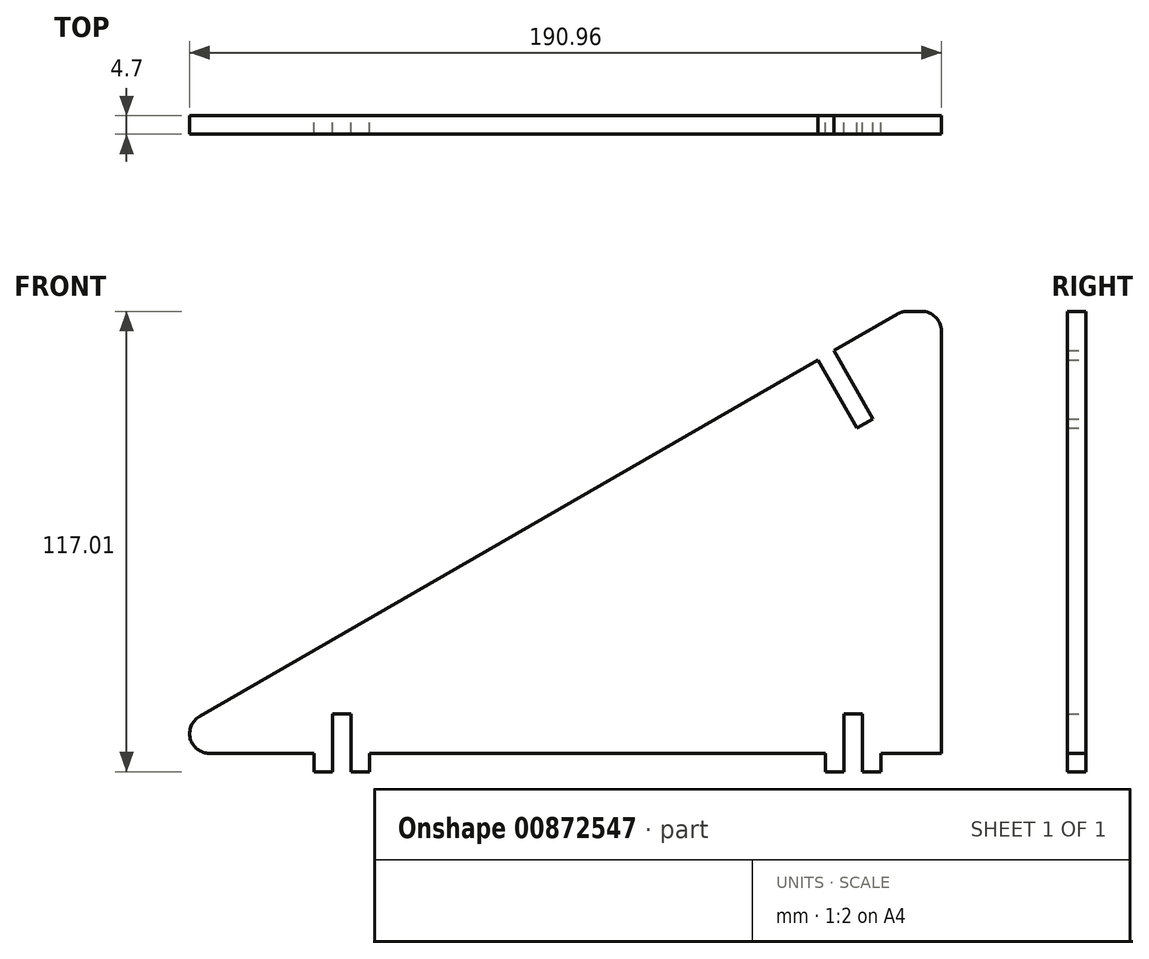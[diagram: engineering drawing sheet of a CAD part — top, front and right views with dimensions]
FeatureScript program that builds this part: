
annotation { "Feature Type Name" : "Feature", "Feature Type Description" : "" }
export const myFeature = defineFeature(function(context is Context, id is Id, definition is map)
    precondition{}
    {
        {
            assignVariable(context, id + "F0", {"name" : "e", "anyValue" : 4.7});
        }
        {
            var Q0;
            Q0=qCreatedBy(makeId("Front.planeOp"),FACE);
            var sketch = newSketch(context, id + "F1", { "sketchPlane" : qUnion([Q0])});
            skLineSegment(sketch, "E0", {"start": v(0, 0) * mm, "end": v(0, 107.3) * mm});
            skLineSegment(sketch, "E1", {"start": v(-5, 112.3) * mm, "end": v(-8.66, 112.3) * mm});
            skLineSegment(sketch, "E2", {"start": v(-11.16, 111.63) * mm, "end": v(-27.32, 102.3) * mm});
            skLineSegment(sketch, "E3", {"start": v(-185.97, 0) * mm, "end": v(-159.4, -0.01) * mm});
            skPoint(sketch, "E4.visualSharp", {"position": v(-204.63, 0) * mm});
            skArc(sketch, "E4.filletArc", {"start": v(-188.46, 9.33) * mm, "mid": v(-190.8, 3.7) * mm, "end": v(-185.97, 0) * mm});
            skPoint(sketch, "E5.visualSharp", {"position": v(0, 112.3) * mm});
            skArc(sketch, "E5.filletArc", {"start": v(0, 107.3) * mm, "mid": v(-1.46, 110.83) * mm, "end": v(-5, 112.3) * mm});
            skPoint(sketch, "E6.visualSharp", {"position": v(-10, 112.3) * mm});
            skArc(sketch, "E6.filletArc", {"start": v(-8.66, 112.3) * mm, "mid": v(-9.95, 112.13) * mm, "end": v(-11.16, 111.63) * mm});
            skLineSegment(sketch, "E7", {"start": v(-31.4, 99.95) * mm, "end": v(-21.4, 82.63) * mm});
            skLineSegment(sketch, "E8", {"start": v(-21.4, 82.63) * mm, "end": v(-17.33, 84.98) * mm});
            skLineSegment(sketch, "E9", {"start": v(-17.33, 84.98) * mm, "end": v(-27.32, 102.3) * mm});
            skLineSegment(sketch, "E10.trimOffspring", {"start": v(-31.4, 99.95) * mm, "end": v(-188.46, 9.33) * mm});
            skLineSegment(sketch, "E11", {"start": v(-154.7, -0.01) * mm, "end": v(-154.7, 9.99) * mm});
            skLineSegment(sketch, "E12", {"start": v(-154.7, 9.99) * mm, "end": v(-150, 9.99) * mm});
            skLineSegment(sketch, "E13", {"start": v(-150, 9.99) * mm, "end": v(-150, -0.01) * mm});
            skLineSegment(sketch, "E14", {"start": v(-24.7, -0.01) * mm, "end": v(-24.7, 9.99) * mm});
            skLineSegment(sketch, "E15", {"start": v(-24.7, 9.99) * mm, "end": v(-20, 9.99) * mm});
            skLineSegment(sketch, "E16", {"start": v(-20, 9.99) * mm, "end": v(-20, 0) * mm});
            skLineSegment(sketch, "E17", {"start": v(-145.3, -0.01) * mm, "end": v(-29.4, -0.01) * mm});
            skLineSegment(sketch, "E18", {"start": v(-150, -0.01) * mm, "end": v(-150, -4.71) * mm});
            skLineSegment(sketch, "E19", {"start": v(-145.3, -0.01) * mm, "end": v(-145.3, -4.71) * mm});
            skLineSegment(sketch, "E20", {"start": v(-145.3, -4.71) * mm, "end": v(-150, -4.71) * mm});
            skLineSegment(sketch, "E21", {"start": v(-159.4, -0.01) * mm, "end": v(-159.4, -4.71) * mm});
            skLineSegment(sketch, "E22", {"start": v(-159.4, -4.71) * mm, "end": v(-154.7, -4.71) * mm});
            skLineSegment(sketch, "E23", {"start": v(-154.7, -4.71) * mm, "end": v(-154.7, -0.01) * mm});
            skLineSegment(sketch, "E24", {"start": v(-15.3, 0) * mm, "end": v(0, 0) * mm});
            skLineSegment(sketch, "E25", {"start": v(-29.4, -0.01) * mm, "end": v(-29.4, -4.71) * mm});
            skLineSegment(sketch, "E26", {"start": v(-24.7, -0.01) * mm, "end": v(-24.7, -4.71) * mm});
            skLineSegment(sketch, "E27", {"start": v(-29.4, -4.71) * mm, "end": v(-24.7, -4.71) * mm});
            skLineSegment(sketch, "E28", {"start": v(-20, 0) * mm, "end": v(-20, -4.7) * mm});
            skLineSegment(sketch, "E29", {"start": v(-15.3, 0) * mm, "end": v(-15.3, -4.7) * mm});
            skLineSegment(sketch, "E30", {"start": v(-20, -4.7) * mm, "end": v(-15.3, -4.7) * mm});
            skSolve(sketch);
        }
        {
            var Q0;
            Q0=makeQuery(id+"F1.imprint","IMPRINT",FACE,{"disambiguationData":[TD([[makeQuery(id+"F1.imprint","IMPRINT",EDGE,{"derivedFrom":sQuery(id+"F1.wireOp",EDGE,"E0")}),1.0]])]});
            extrude(context, id + "F2", {"entities" : qUnion([Q0]), "depth" : (getVariable(context, 'e')) * mm, "offsetDistance" : 25 * mm});
        }
    });
